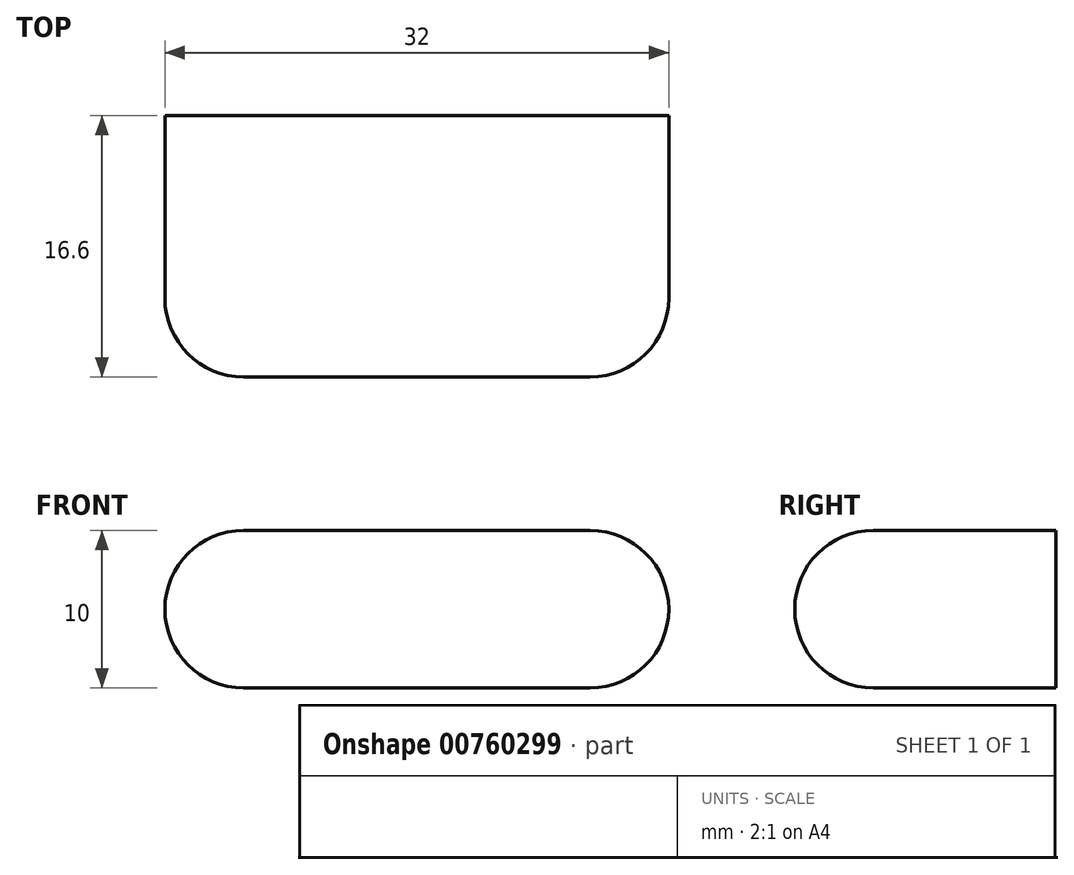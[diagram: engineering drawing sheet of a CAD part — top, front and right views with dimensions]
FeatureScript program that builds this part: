
annotation { "Feature Type Name" : "Feature", "Feature Type Description" : "" }
export const myFeature = defineFeature(function(context is Context, id is Id, definition is map)
    precondition{}
    {
        {
            var Q0;
            Q0=qCreatedBy(makeId("Front.planeOp"),FACE);
            var sketch = newSketch(context, id + "F0", { "sketchPlane" : qUnion([Q0])});
            skLineSegment(sketch, "E0.bottom", {"start": v(16, -5) * mm, "end": v(-16, -5) * mm});
            skLineSegment(sketch, "E0.top", {"start": v(16, 5) * mm, "end": v(-16, 5) * mm});
            skLineSegment(sketch, "E0.left", {"start": v(16, -5) * mm, "end": v(16, 5) * mm});
            skLineSegment(sketch, "E0.right", {"start": v(-16, -5) * mm, "end": v(-16, 5) * mm});
            skPoint(sketch, "E0.middle", {"position": v(0, 0) * mm});
            skSolve(sketch);
        }
        {
            var Q0;
            Q0=makeQuery(id+"F0.imprint","IMPRINT",FACE,{"disambiguationData":[TD([[makeQuery(id+"F0.imprint","IMPRINT",EDGE,{"derivedFrom":sQuery(id+"F0.wireOp",EDGE,"E0.bottom")}),-1.0]])]});
            extrude(context, id + "F1", {"entities" : qUnion([Q0]), "depth" : 16.6 * mm, "offsetDistance" : 25 * mm});
        }
        {
            var Q0;
            Q0=makeQuery(id+"F1.opExtrude","SWEPT_EDGE",EDGE,{"disambiguationData":[OSD([sQuery(id+"F0.wireOp",EDGE,"E0.top"),sQuery(id+"F0.wireOp",EDGE,"E0.left")])]});
            fillet(context, id + "F2", {"entities" : qUnion([Q0]), "radius" : 5 * mm, "tangentPropagation" : true, "allowEdgeOverflow" : false});
        }
        {
            var Q0;
            Q0=makeQuery(id+"F1.opExtrude","SWEPT_EDGE",EDGE,{"disambiguationData":[OSD([sQuery(id+"F0.wireOp",EDGE,"E0.top"),sQuery(id+"F0.wireOp",EDGE,"E0.right")])]});
            var Q1;
            Q1=makeQuery(id+"F1.opExtrude","SWEPT_EDGE",EDGE,{"disambiguationData":[OSD([sQuery(id+"F0.wireOp",EDGE,"E0.bottom"),sQuery(id+"F0.wireOp",EDGE,"E0.left")])]});
            var Q2;
            Q2=makeQuery(id+"F1.opExtrude","SWEPT_EDGE",EDGE,{"disambiguationData":[OSD([sQuery(id+"F0.wireOp",EDGE,"E0.bottom"),sQuery(id+"F0.wireOp",EDGE,"E0.right")])]});
            fillet(context, id + "F3", {"entities" : qUnion([Q0, Q1, Q2]), "radius" : 5 * mm, "tangentPropagation" : true, "allowEdgeOverflow" : false});
        }
        {
            var Q0;
            Q0=makeQuery(id+"F1.opExtrude","CAP_EDGE",EDGE,{"disambiguationData":[OSD([sQuery(id+"F0.wireOp",EDGE,"E0.top")])],"isStart":false});
            fillet(context, id + "F4", {"entities" : qUnion([Q0]), "radius" : 5 * mm, "tangentPropagation" : true, "allowEdgeOverflow" : false});
        }
    });
